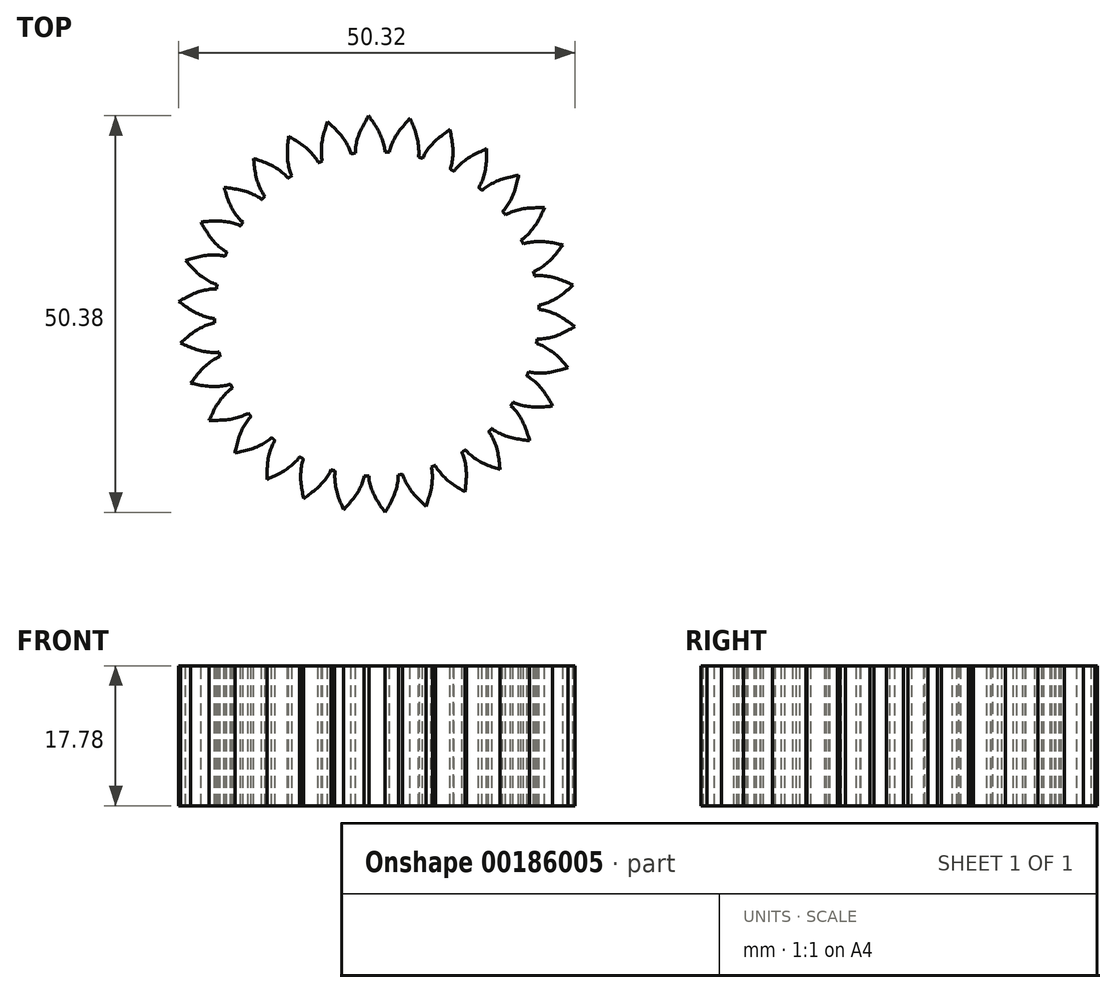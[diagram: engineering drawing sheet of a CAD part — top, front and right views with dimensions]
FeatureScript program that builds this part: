
annotation { "Feature Type Name" : "Feature", "Feature Type Description" : "" }
export const myFeature = defineFeature(function(context is Context, id is Id, definition is map)
    precondition{}
    {
        {
            assignVariable(context, id + "F0", {"name" : "nt", "anyValue" : 30});
        }
        {
            var Q0;
            Q0=qCreatedBy(makeId("Top.planeOp"),FACE);
            var sketch = newSketch(context, id + "F1", { "sketchPlane" : qUnion([Q0])});
            skPoint(sketch, "E0", {"position": v(1.08, 20.6) * mm});
            skPoint(sketch, "E1", {"position": v(1.06, 20.92) * mm});
            skPoint(sketch, "E2", {"position": v(0.84, 21.88) * mm});
            skPoint(sketch, "E3", {"position": v(0.2, 23.39) * mm});
            skPoint(sketch, "E4", {"position": v(-1.05, 25.3) * mm});
            skCircle(sketch, "E5", {"center": v(0, 0) * mm, "radius": 20.62 * mm});
            skCircle(sketch, "E6", {"center": v(0, 0) * mm, "radius": 23.81 * mm, "construction": true});
            skCircle(sketch, "E7", {"center": v(0, 0) * mm, "radius": 30.2 * mm});
            skCircle(sketch, "E8", {"center": v(0, 0) * mm, "radius": 25.33 * mm});
            skFitSpline(sketch, "E9", {"points": [v(1.08, 20.6) * mm, v(1.06, 20.92) * mm, v(0.84, 21.88) * mm, v(0.2, 23.39) * mm, v(-1.05, 25.3) * mm], "startDerivative": vector(-0.05, 2.19) * mm, "endDerivative": vector(-3.92, 5.61) * mm});
            skLineSegment(sketch, "E10", {"start": v(-1.05, 25.3) * mm, "end": v(-0.85, 20.6) * mm});
            skSolve(sketch);
        }
        {
            var Q0;
            {var subQ1=sQuery(id+"F1.wireOp",EDGE,"E9");Q0=makeQuery(id+"F1.imprint","IMPRINT",FACE,{"disambiguationData":[TD([[makeQuery(id+"F1.imprint","IMPRINT",EDGE,{"derivedFrom":subQ1}),1.0]])]});}
            extrude(context, id + "F2", {"entities" : qUnion([Q0]), "depth" : 25.4 * mm});
        }
        {
            var Q0;
            Q0=makeQuery(id+"F2.opExtrude","CAP_FACE",FACE,{"disambiguationData":[OSD([sQuery(id+"F1.wireOp",EDGE,"E5"),sQuery(id+"F1.wireOp",EDGE,"E9"),sQuery(id+"F1.wireOp",EDGE,"E10")])],"isStart":false});
            var sketch = newSketch(context, id + "F3", { "sketchPlane" : qUnion([Q0])});
            skFitSpline(sketch, "E11.0", {"points": [v(1.08, 20.6) * mm, v(1.08, 20.69) * mm, v(1.07, 20.95) * mm, v(0.85, 21.96) * mm, v(0.25, 23.46) * mm, v(-0.6, 24.66) * mm, v(-1.05, 25.3) * mm]});
            skFitSpline(sketch, "E12.0", {"points": [v(1.02, 20.6) * mm, v(1.01, 20.68) * mm, v(1.01, 20.86) * mm, v(0.92, 21.34) * mm, v(0.76, 21.93) * mm, v(0.54, 22.56) * mm, v(0.24, 23.2) * mm, v(-0.15, 23.88) * mm, v(-0.6, 24.57) * mm, v(-0.94, 25.04) * mm, v(-1.1, 25.27) * mm]});
            skLineSegment(sketch, "E13", {"start": v(-1.05, 25.3) * mm, "end": v(-1.1, 25.27) * mm});
            skLineSegment(sketch, "E14", {"start": v(1.08, 20.6) * mm, "end": v(1.02, 20.6) * mm});
            skSolve(sketch);
        }
        {
            var Q0;
            {var subQ3=sQuery(id+"F3.wireOp",EDGE,"E11.0");Q0=makeQuery(id+"F3.imprint","IMPRINT",FACE,{"disambiguationData":[TD([[makeQuery(id+"F3.imprint","IMPRINT",EDGE,{"derivedFrom":subQ3}),1.0]])]});}
            extrude(context, id + "F4", {"entities" : qUnion([Q0]), "operationType" : NewBodyOperationType.REMOVE, "endBound" : BoundingType.THROUGH_ALL, "oppositeDirection" : true, "depth" : 25.4 * mm});
        }
        {
            var Q0;
            Q0=makeQuery(id+"F2.opExtrude","SWEPT_BODY",BODY,{"disambiguationData":[OSD([sQuery(id+"F1.wireOp",EDGE,"E5"),sQuery(id+"F1.wireOp",EDGE,"E9"),sQuery(id+"F1.wireOp",EDGE,"E10")])]});
            var Q1;
            Q1=makeQuery(id+"F2.opExtrude","SWEPT_FACE",FACE,{"disambiguationData":[OSD([sQuery(id+"F1.wireOp",EDGE,"E10")])]});
            mirror(context, id + "F5", {"operationType" : NewBodyOperationType.ADD, "entities" : qUnion([Q0]), "mirrorPlane" : qUnion([Q1])});
        }
        {
            var Q0;
            {var subQ0=makeQuery(id+"F2.opExtrude","CAP_FACE",FACE,{"disambiguationData":[OSD([sQuery(id+"F1.wireOp",EDGE,"E5"),sQuery(id+"F1.wireOp",EDGE,"E9"),sQuery(id+"F1.wireOp",EDGE,"E10")])],"isStart":false});Q0=makeQuery(id+"F5.boolean.opBoolean","MERGE",FACE,{"derivedFrom":[subQ0,makeQuery(id+"F5.opPattern","COPY",FACE,{"derivedFrom":subQ0,"instanceName":"1"})]});}
            var sketch = newSketch(context, id + "F6", { "sketchPlane" : qUnion([Q0])});
            skCircle(sketch, "E15", {"center": v(0, 0) * mm, "radius": 20.62 * mm});
            skSolve(sketch);
        }
        {
            var Q0;
            Q0=qSketchRegion(id+"F6",true);
            var Q1;
            {var subQ0=makeQuery(id+"F2.opExtrude","CAP_FACE",FACE,{"disambiguationData":[OSD([sQuery(id+"F1.wireOp",EDGE,"E5"),sQuery(id+"F1.wireOp",EDGE,"E9"),sQuery(id+"F1.wireOp",EDGE,"E10")])],"isStart":true});Q1=makeQuery(id+"F5.boolean.opBoolean","MERGE",FACE,{"derivedFrom":[subQ0,makeQuery(id+"F5.opPattern","COPY",FACE,{"derivedFrom":subQ0,"instanceName":"1"})]});}
            extrude(context, id + "F7", {"entities" : qUnion([Q0]), "endBound" : BoundingType.UP_TO_SURFACE, "oppositeDirection" : true, "endBoundEntityFace" : qUnion([Q1]), "depth" : 25.4 * mm});
        }
        {
            var Q0;
            Q0=makeQuery(id+"F2.opExtrude","SWEPT_BODY",BODY,{"disambiguationData":[OSD([sQuery(id+"F1.wireOp",EDGE,"E5"),sQuery(id+"F1.wireOp",EDGE,"E9"),sQuery(id+"F1.wireOp",EDGE,"E10")])]});
            var Q1;
            {var subQ0=makeQuery(id+"F2.opExtrude","SWEPT_FACE",FACE,{"disambiguationData":[OSD([sQuery(id+"F1.wireOp",EDGE,"E5")])]});Q1=makeQuery(id+"F5.boolean.opBoolean","MERGE",FACE,{"derivedFrom":[subQ0,makeQuery(id+"F5.opPattern","COPY",FACE,{"derivedFrom":subQ0,"instanceName":"1"})]});}
            circularPattern(context, id + "F8", {"operationType" : NewBodyOperationType.ADD, "entities" : qUnion([Q0]), "axis" : qUnion([Q1]), "angle" : 360 * degree, "instanceCount" : getVariable(context, 'nt'), "equalSpace" : true});
        }
        {
            var Q0;
            {var subQ0=makeQuery(id+"F2.opExtrude","CAP_FACE",FACE,{"disambiguationData":[OSD([sQuery(id+"F1.wireOp",EDGE,"E5"),sQuery(id+"F1.wireOp",EDGE,"E9"),sQuery(id+"F1.wireOp",EDGE,"E10")])],"isStart":false});var subQ1=makeQuery(id+"F5.boolean.opBoolean","MERGE",FACE,{"derivedFrom":[subQ0,makeQuery(id+"F5.opPattern","COPY",FACE,{"derivedFrom":subQ0,"instanceName":"1"})]});Q0=makeQuery(id+"F8.boolean.opBoolean","MERGE",FACE,{"derivedFrom":[subQ1,makeQuery(id+"F7.opExtrude","CAP_FACE",FACE,{"disambiguationData":[OSD([sQuery(id+"F6.wireOp",EDGE,"E15")])],"isStart":true}),makeQuery(id+"F8.opPattern","COPY",FACE,{"derivedFrom":subQ1,"instanceName":"1"}),makeQuery(id+"F8.opPattern","COPY",FACE,{"derivedFrom":subQ1,"instanceName":"2"}),makeQuery(id+"F8.opPattern","COPY",FACE,{"derivedFrom":subQ1,"instanceName":"3"}),makeQuery(id+"F8.opPattern","COPY",FACE,{"derivedFrom":subQ1,"instanceName":"4"}),makeQuery(id+"F8.opPattern","COPY",FACE,{"derivedFrom":subQ1,"instanceName":"5"}),makeQuery(id+"F8.opPattern","COPY",FACE,{"derivedFrom":subQ1,"instanceName":"6"}),makeQuery(id+"F8.opPattern","COPY",FACE,{"derivedFrom":subQ1,"instanceName":"7"}),makeQuery(id+"F8.opPattern","COPY",FACE,{"derivedFrom":subQ1,"instanceName":"8"}),makeQuery(id+"F8.opPattern","COPY",FACE,{"derivedFrom":subQ1,"instanceName":"9"}),makeQuery(id+"F8.opPattern","COPY",FACE,{"derivedFrom":subQ1,"instanceName":"10"}),makeQuery(id+"F8.opPattern","COPY",FACE,{"derivedFrom":subQ1,"instanceName":"11"}),makeQuery(id+"F8.opPattern","COPY",FACE,{"derivedFrom":subQ1,"instanceName":"12"}),makeQuery(id+"F8.opPattern","COPY",FACE,{"derivedFrom":subQ1,"instanceName":"13"}),makeQuery(id+"F8.opPattern","COPY",FACE,{"derivedFrom":subQ1,"instanceName":"14"}),makeQuery(id+"F8.opPattern","COPY",FACE,{"derivedFrom":subQ1,"instanceName":"15"}),makeQuery(id+"F8.opPattern","COPY",FACE,{"derivedFrom":subQ1,"instanceName":"16"}),makeQuery(id+"F8.opPattern","COPY",FACE,{"derivedFrom":subQ1,"instanceName":"17"}),makeQuery(id+"F8.opPattern","COPY",FACE,{"derivedFrom":subQ1,"instanceName":"18"}),makeQuery(id+"F8.opPattern","COPY",FACE,{"derivedFrom":subQ1,"instanceName":"19"}),makeQuery(id+"F8.opPattern","COPY",FACE,{"derivedFrom":subQ1,"instanceName":"20"}),makeQuery(id+"F8.opPattern","COPY",FACE,{"derivedFrom":subQ1,"instanceName":"21"}),makeQuery(id+"F8.opPattern","COPY",FACE,{"derivedFrom":subQ1,"instanceName":"22"}),makeQuery(id+"F8.opPattern","COPY",FACE,{"derivedFrom":subQ1,"instanceName":"23"}),makeQuery(id+"F8.opPattern","COPY",FACE,{"derivedFrom":subQ1,"instanceName":"24"}),makeQuery(id+"F8.opPattern","COPY",FACE,{"derivedFrom":subQ1,"instanceName":"25"}),makeQuery(id+"F8.opPattern","COPY",FACE,{"derivedFrom":subQ1,"instanceName":"26"}),makeQuery(id+"F8.opPattern","COPY",FACE,{"derivedFrom":subQ1,"instanceName":"27"}),makeQuery(id+"F8.opPattern","COPY",FACE,{"derivedFrom":subQ1,"instanceName":"28"}),makeQuery(id+"F8.opPattern","COPY",FACE,{"derivedFrom":subQ1,"instanceName":"29"})]});}
            extrude(context, id + "F9", {"entities" : qUnion([Q0]), "operationType" : NewBodyOperationType.ADD, "depth" : 17.78 * mm});
        }
        {
            var Q0;
            Q0=makeQuery(id+"F9.opExtrude","CAP_FACE",FACE,{"disambiguationData":[OSD([sQuery(id+"F1.wireOp",EDGE,"E5"),sQuery(id+"F1.wireOp",EDGE,"E9"),sQuery(id+"F1.wireOp",EDGE,"E10"),sQuery(id+"F6.wireOp",EDGE,"E15")])],"isStart":false});
            extrude(context, id + "F10", {"entities" : qUnion([Q0]), "operationType" : NewBodyOperationType.REMOVE, "oppositeDirection" : true, "depth" : 25.4 * mm});
        }
        {
            var Q0;
            Q0=makeQuery(id+"F10.boolean.opBoolean","COPY",FACE,{"derivedFrom":makeQuery(id+"F10.opExtrude","CAP_FACE",FACE,{"disambiguationData":[OSD([sQuery(id+"F1.wireOp",EDGE,"E5"),sQuery(id+"F1.wireOp",EDGE,"E9"),sQuery(id+"F1.wireOp",EDGE,"E10"),sQuery(id+"F6.wireOp",EDGE,"E15")])],"isStart":false})});
            extrude(context, id + "F11", {"entities" : qUnion([Q0]), "operationType" : NewBodyOperationType.ADD, "depth" : 12.7 * mm});
        }
        {
            var Q0;
            Q0=makeQuery(id+"F11.opExtrude","CAP_FACE",FACE,{"disambiguationData":[OSD([sQuery(id+"F1.wireOp",EDGE,"E5"),sQuery(id+"F1.wireOp",EDGE,"E9"),sQuery(id+"F1.wireOp",EDGE,"E10"),sQuery(id+"F6.wireOp",EDGE,"E15")])],"isStart":false});
            extrude(context, id + "F12", {"entities" : qUnion([Q0]), "operationType" : NewBodyOperationType.REMOVE, "oppositeDirection" : true, "depth" : 12.7 * mm});
        }
    });
